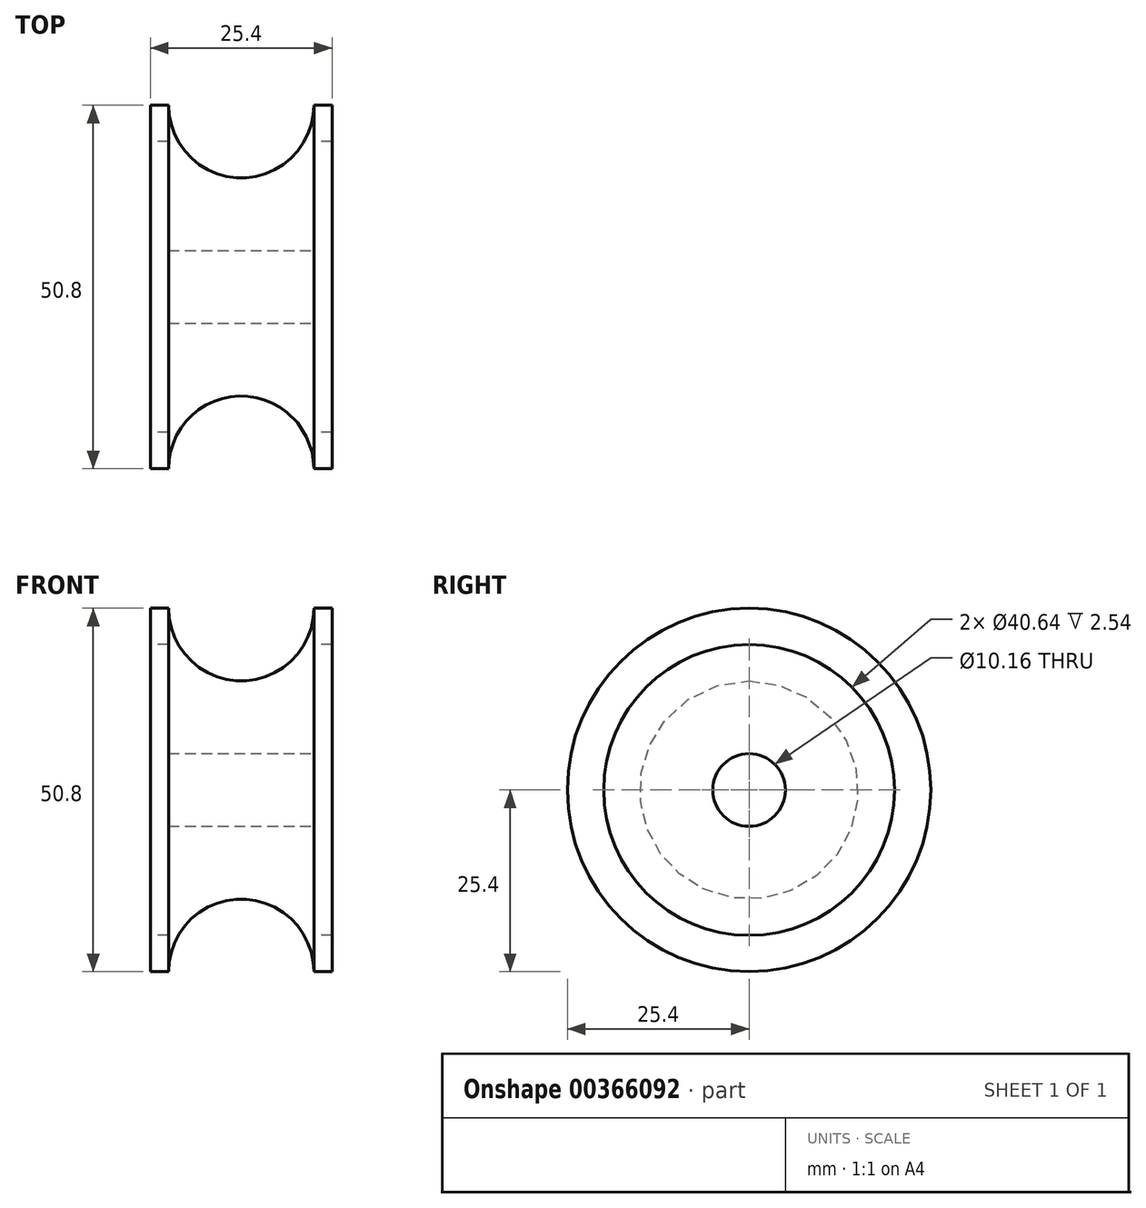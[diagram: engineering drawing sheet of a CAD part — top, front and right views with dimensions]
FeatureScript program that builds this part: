
annotation { "Feature Type Name" : "Feature", "Feature Type Description" : "" }
export const myFeature = defineFeature(function(context is Context, id is Id, definition is map)
    precondition{}
    {
        {
            var Q0;
            Q0=qCreatedBy(makeId("Top.planeOp"),FACE);
            var sketch = newSketch(context, id + "F0", { "sketchPlane" : qUnion([Q0])});
            skLineSegment(sketch, "E0.bottom", {"start": v(12.7, 25.4) * mm, "end": v(10.16, 25.4) * mm});
            skLineSegment(sketch, "E0.left", {"start": v(12.7, 25.4) * mm, "end": v(12.7, 20.32) * mm});
            skLineSegment(sketch, "E0.right", {"start": v(-12.7, 25.4) * mm, "end": v(-12.7, 20.32) * mm});
            skPoint(sketch, "E0.middle", {"position": v(0, 0) * mm});
            skArc(sketch, "E1", {"start": v(10.16, 25.4) * mm, "mid": v(0, 15.24) * mm, "end": v(-10.16, 25.4) * mm});
            skLineSegment(sketch, "E2.trimOffspring", {"start": v(-10.16, 25.4) * mm, "end": v(-12.7, 25.4) * mm});
            skLineSegment(sketch, "E3", {"start": v(-10.16, 0) * mm, "end": v(10.16, 0) * mm});
            skPoint(sketch, "E4.trimOffspring.end.orphan", {"position": v(-12.7, -25.4) * mm});
            skPoint(sketch, "E4.trimOffspring.start.orphan", {"position": v(-10.16, -25.4) * mm});
            skPoint(sketch, "E0.top.end.orphan", {"position": v(10.16, -25.4) * mm});
            skPoint(sketch, "E5.orphan", {"position": v(12.7, -25.4) * mm});
            skLineSegment(sketch, "E6", {"start": v(-26.88, 0) * mm, "end": v(-12.7, 0) * mm, "construction": true});
            skLineSegment(sketch, "E7", {"start": v(12.7, 20.32) * mm, "end": v(10.16, 20.32) * mm});
            skLineSegment(sketch, "E8", {"start": v(10.16, 20.32) * mm, "end": v(10.16, 0) * mm});
            skLineSegment(sketch, "E9", {"start": v(-12.7, 20.32) * mm, "end": v(-10.16, 20.32) * mm});
            skLineSegment(sketch, "E10", {"start": v(-10.16, 20.32) * mm, "end": v(-10.16, 0) * mm});
            skLineSegment(sketch, "E11.trimOffspring", {"start": v(-10.16, 0) * mm, "end": v(10.16, 0) * mm, "construction": true});
            skLineSegment(sketch, "E12.trimOffspring", {"start": v(12.7, 0) * mm, "end": v(32.82, 0) * mm, "construction": true});
            skSolve(sketch);
        }
        {
            var Q0;
            Q0=qCreatedBy(makeId("Top.planeOp"),FACE);
            var sketch = newSketch(context, id + "F1", { "sketchPlane" : qUnion([Q0])});
            skLineSegment(sketch, "E13", {"start": v(-70.28, 0) * mm, "end": v(42.11, 0) * mm});
            skSolve(sketch);
        }
        {
            var Q0;
            Q0=makeQuery(id+"F0.imprint","IMPRINT",FACE,{"disambiguationData":[TD([[makeQuery(id+"F0.imprint","IMPRINT",EDGE,{"derivedFrom":sQuery(id+"F0.wireOp",EDGE,"E0.bottom")}),1.0]])]});
            var Q1;
            Q1=sQuery(id+"F1.wireOp",EDGE,"E13");
            revolve(context, id + "F2", {"entities" : qUnion([Q0]), "axis" : qUnion([Q1]), "revolveType" : RevolveType.FULL});
        }
        {
            var Q0;
            Q0=makeQuery(id+"F2.opRevolve","SWEPT_FACE",FACE,{"disambiguationData":[OSD([sQuery(id+"F0.wireOp",EDGE,"E0.left")])]});
            var sketch = newSketch(context, id + "F3", { "sketchPlane" : qUnion([Q0])});
            skCircle(sketch, "E14", {"center": v(0, 0) * mm, "radius": 5.08 * mm});
            skSolve(sketch);
        }
        {
            var Q0;
            Q0=sQuery(id+"F3.wireOp",VERTEX,"E14.center");
            var Q1;
            Q1=makeQuery(id+"F2.opRevolve","SWEPT_BODY",BODY,{"disambiguationData":[OSD([sQuery(id+"F0.wireOp",EDGE,"E0.bottom"),sQuery(id+"F0.wireOp",EDGE,"E0.left"),sQuery(id+"F0.wireOp",EDGE,"E0.right"),sQuery(id+"F0.wireOp",EDGE,"E1"),sQuery(id+"F0.wireOp",EDGE,"E2.trimOffspring"),sQuery(id+"F0.wireOp",EDGE,"E3")])]});
            hole(context, id + "F4", {"style" : HoleStyle.SIMPLE, "endStyle" : HoleEndStyle.THROUGH, "holeDiameter" : 10.16 * mm, "isTappedThrough" : true, "tappedDepth" : 12.7 * mm, "tapClearance" : 3, "locations" : qUnion([Q0]), "scope" : qUnion([Q1])});
        }
    });
